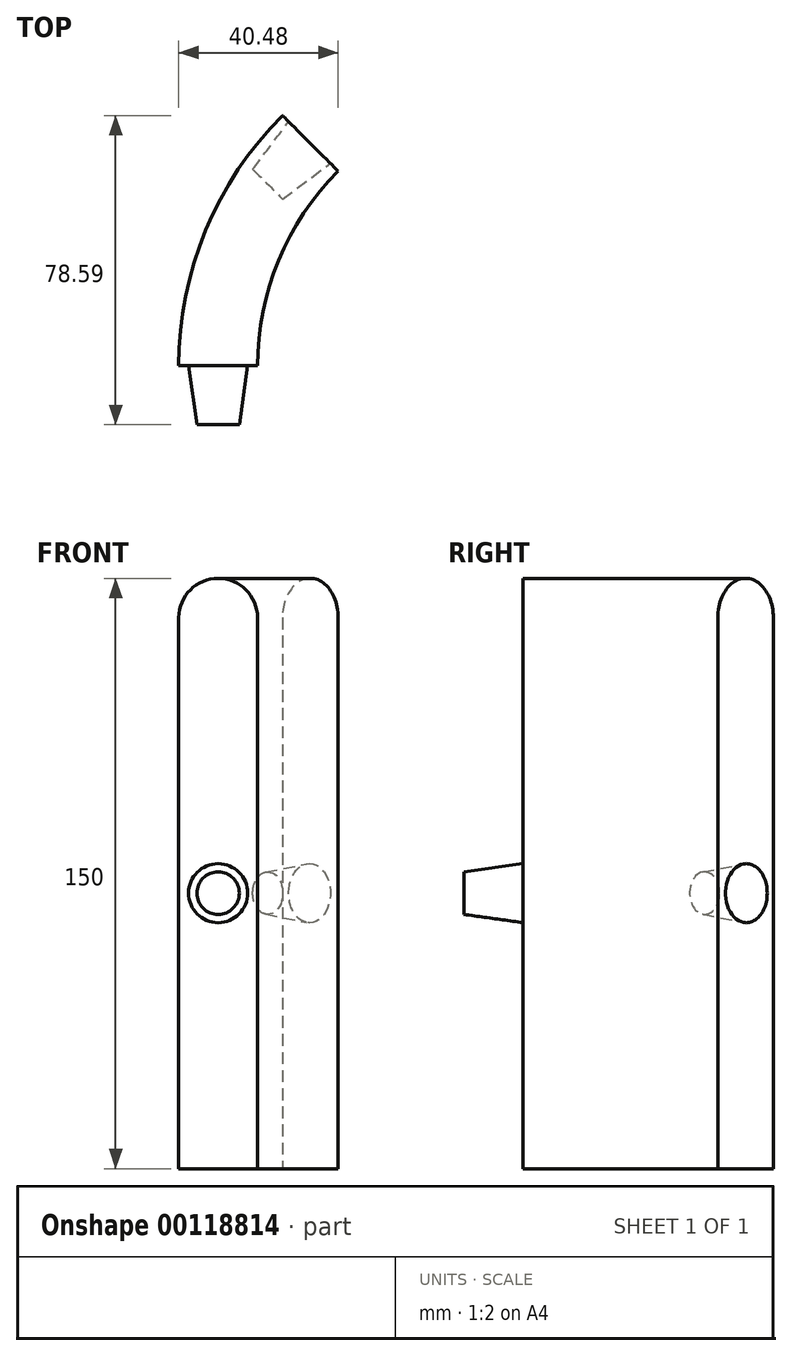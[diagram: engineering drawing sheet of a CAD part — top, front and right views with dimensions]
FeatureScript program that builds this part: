
annotation { "Feature Type Name" : "Feature", "Feature Type Description" : "" }
export const myFeature = defineFeature(function(context is Context, id is Id, definition is map)
    precondition{}
    {
        {
            var Q0;
            Q0=qCreatedBy(makeId("Front.planeOp"),FACE);
            var sketch = newSketch(context, id + "F0", { "sketchPlane" : qUnion([Q0])});
            skLineSegment(sketch, "E0", {"start": v(127.32, 299.12) * mm, "end": v(127.32, 149.12) * mm});
            skLineSegment(sketch, "E1", {"start": v(127.32, 299.12) * mm, "end": v(37.4, 299.12) * mm});
            skLineSegment(sketch, "E2", {"start": v(37.4, 299.12) * mm, "end": v(37.4, 149.12) * mm});
            skLineSegment(sketch, "E3", {"start": v(37.4, 149.12) * mm, "end": v(127.32, 149.12) * mm});
            skSolve(sketch);
        }
        {
            var Q0;
            Q0=makeQuery(id+"F0.imprint","IMPRINT",FACE,{"disambiguationData":[TD([[makeQuery(id+"F0.imprint","IMPRINT",EDGE,{"derivedFrom":sQuery(id+"F0.wireOp",EDGE,"qIKZoeJY-TQep-c7Ri-jmz6-qnDqXJ4BGPkj")}),1.0]])]});
            var Q1;
            Q1=makeQuery(id+"F0.imprint","IMPRINT",FACE,{"disambiguationData":[TD([[makeQuery(id+"F0.imprint","IMPRINT",EDGE,{"derivedFrom":sQuery(id+"F0.wireOp",EDGE,"E0")}),-1.0]])]});
            var Q2;
            Q2=sQuery(id+"F0.wireOp",EDGE,"E0");
            revolve(context, id + "F1", {"entities" : qUnion([Q0, Q1]), "axis" : qUnion([Q2]), "revolveType" : RevolveType.ONE_DIRECTION, "angle" : 45 * degree});
        }
        {
            var Q0;
            Q0=makeQuery(id+"F1.opRevolve","CAP_FACE",FACE,{"disambiguationData":[OSD([sQuery(id+"F0.wireOp",EDGE,"c1a47f16-03cb-4326-a7fb-4da27e49267e"),sQuery(id+"F0.wireOp",EDGE,"0445b6aa-1599-4f51-a42e-cd0f4c540e00"),sQuery(id+"F0.wireOp",EDGE,"2b562399-184e-4d8c-bb95-a8394558efe5.trimOffspring"),sQuery(id+"F0.wireOp",EDGE,"qIKZoeJY-TQep-c7Ri-jmz6-qnDqXJ4BGPkj"),sQuery(id+"F0.wireOp",EDGE,"5GoxPhpb-W2qU-YVQz-mgj7-7G05RjJSTRpR"),sQuery(id+"F0.wireOp",EDGE,"W7TmGzvV-SRVJ-wapx-RxKG-6s7Lfqn86I50"),sQuery(id+"F0.wireOp",EDGE,"FrPlEDyA-e7Am-JMK7-J0is-8kwWFS23w3qv")])],"isStart":false});
            var Q1;
            Q1=makeQuery(id+"F1.opRevolve","CAP_FACE",FACE,{"disambiguationData":[OSD([sQuery(id+"F0.wireOp",EDGE,"c1a47f16-03cb-4326-a7fb-4da27e49267e"),sQuery(id+"F0.wireOp",EDGE,"0445b6aa-1599-4f51-a42e-cd0f4c540e00"),sQuery(id+"F0.wireOp",EDGE,"2b562399-184e-4d8c-bb95-a8394558efe5.trimOffspring"),sQuery(id+"F0.wireOp",EDGE,"qIKZoeJY-TQep-c7Ri-jmz6-qnDqXJ4BGPkj"),sQuery(id+"F0.wireOp",EDGE,"5GoxPhpb-W2qU-YVQz-mgj7-7G05RjJSTRpR"),sQuery(id+"F0.wireOp",EDGE,"W7TmGzvV-SRVJ-wapx-RxKG-6s7Lfqn86I50"),sQuery(id+"F0.wireOp",EDGE,"FrPlEDyA-e7Am-JMK7-J0is-8kwWFS23w3qv")])],"isStart":true});
            var Q2;
            Q2=makeQuery(id+"F1.opRevolve","SWEPT_FACE",FACE,{"disambiguationData":[OSD([sQuery(id+"F0.wireOp",EDGE,"qIKZoeJY-TQep-c7Ri-jmz6-qnDqXJ4BGPkj")])]});
            var Q3;
            Q3=makeQuery(id+"F1.opRevolve","SWEPT_FACE",FACE,{"disambiguationData":[OSD([sQuery(id+"F0.wireOp",EDGE,"FrPlEDyA-e7Am-JMK7-J0is-8kwWFS23w3qv")])]});
            var Q4;
            Q4=makeQuery(id+"F1.opRevolve","SWEPT_FACE",FACE,{"disambiguationData":[OSD([sQuery(id+"F0.wireOp",EDGE,"Zfw3s35M-H7I7-ctV8-WwCO-TXvZiI164tsA")])]});
            var Q5;
            Q5=makeQuery(id+"F1.opRevolve","SWEPT_FACE",FACE,{"disambiguationData":[OSD([sQuery(id+"F0.wireOp",EDGE,"DxNpelhW-NPha-Za65-5rby-Dc9gSIxmAqf3")])]});
            var Q6;
            Q6=makeQuery(id+"F1.opRevolve","CAP_FACE",FACE,{"disambiguationData":[OSD([sQuery(id+"F0.wireOp",EDGE,"E0"),sQuery(id+"F0.wireOp",EDGE,"h8w9ds9V-v6di-2uzp-dC4j-q0jaSeQ5vev1"),sQuery(id+"F0.wireOp",EDGE,"rqYKbdp3-fYyZ-YRGA-wxHp-ysZJsVzrtoBV"),sQuery(id+"F0.wireOp",EDGE,"CGmn5kAD-aOFs-twpu-ufA2-BfELl45xMEkJ")])],"isStart":true});
            var Q7;
            Q7=makeQuery(id+"F1.opRevolve","CAP_FACE",FACE,{"disambiguationData":[OSD([sQuery(id+"F0.wireOp",EDGE,"E0"),sQuery(id+"F0.wireOp",EDGE,"h8w9ds9V-v6di-2uzp-dC4j-q0jaSeQ5vev1"),sQuery(id+"F0.wireOp",EDGE,"rqYKbdp3-fYyZ-YRGA-wxHp-ysZJsVzrtoBV"),sQuery(id+"F0.wireOp",EDGE,"CGmn5kAD-aOFs-twpu-ufA2-BfELl45xMEkJ")])],"isStart":false});
            var Q8;
            Q8=makeQuery(id+"F1.opRevolve","SWEPT_FACE",FACE,{"disambiguationData":[OSD([sQuery(id+"F0.wireOp",EDGE,"CGmn5kAD-aOFs-twpu-ufA2-BfELl45xMEkJ")])]});
            var Q9;
            Q9=makeQuery(id+"F1.opRevolve","SWEPT_FACE",FACE,{"disambiguationData":[OSD([sQuery(id+"F0.wireOp",EDGE,"rqYKbdp3-fYyZ-YRGA-wxHp-ysZJsVzrtoBV")])]});
            var Q10;
            Q10=makeQuery(id+"F1.opRevolve","SWEPT_FACE",FACE,{"disambiguationData":[OSD([sQuery(id+"F0.wireOp",EDGE,"E3")])]});
            var Q11;
            Q11=makeQuery(id+"F1.opRevolve","SWEPT_FACE",FACE,{"disambiguationData":[OSD([sQuery(id+"F0.wireOp",EDGE,"E1")])]});
            shell(context, id + "F2", {"entities" : qUnion([Q0, Q1, Q2, Q3, Q4, Q5, Q6, Q7, Q8, Q9, Q10, Q11]), "thickness" : 20 * mm});
        }
        {
            var Q0;
            Q0=makeQuery(id+"F1.opRevolve","CAP_FACE",FACE,{"disambiguationData":[OSD([sQuery(id+"F0.wireOp",EDGE,"E0"),sQuery(id+"F0.wireOp",EDGE,"h8w9ds9V-v6di-2uzp-dC4j-q0jaSeQ5vev1"),sQuery(id+"F0.wireOp",EDGE,"rqYKbdp3-fYyZ-YRGA-wxHp-ysZJsVzrtoBV"),sQuery(id+"F0.wireOp",EDGE,"CGmn5kAD-aOFs-twpu-ufA2-BfELl45xMEkJ")])],"isStart":true});
            var sketch = newSketch(context, id + "F3", { "sketchPlane" : qUnion([Q0])});
            skCircle(sketch, "E4", {"center": v(47.4, 219.12) * mm, "radius": 7.5 * mm});
            skSolve(sketch);
        }
        {
            var Q0;
            Q0 = qSketchRegion(id + "F3", true);
            extrude(context, id + "F4", {"entities" : qUnion([Q0]), "operationType" : NewBodyOperationType.ADD, "depth" : 15 * mm, "hasDraft" : true, "draftAngle" : 8 * degree, "draftPullDirection" : true});
        }
        {
            var Q0;
            Q0=makeQuery(id+"F1.opRevolve","CAP_FACE",FACE,{"disambiguationData":[OSD([sQuery(id+"F0.wireOp",EDGE,"E0"),sQuery(id+"F0.wireOp",EDGE,"h8w9ds9V-v6di-2uzp-dC4j-q0jaSeQ5vev1"),sQuery(id+"F0.wireOp",EDGE,"rqYKbdp3-fYyZ-YRGA-wxHp-ysZJsVzrtoBV"),sQuery(id+"F0.wireOp",EDGE,"CGmn5kAD-aOFs-twpu-ufA2-BfELl45xMEkJ")])],"isStart":false});
            var sketch = newSketch(context, id + "F5", { "sketchPlane" : qUnion([Q0])});
            skCircle(sketch, "E5", {"center": v(-9.82, 219.12) * mm, "radius": 7.5 * mm});
            skSolve(sketch);
        }
        {
            var Q0;
            Q0 = qSketchRegion(id + "F5", true);
            extrude(context, id + "F6", {"entities" : qUnion([Q0]), "operationType" : NewBodyOperationType.REMOVE, "oppositeDirection" : true, "depth" : 15 * mm, "hasDraft" : true, "draftAngle" : 8 * degree, "draftPullDirection" : true});
        }
        {
            var Q0;
            Q0=makeQuery(id+"F1.opRevolve","SWEPT_EDGE",EDGE,{"disambiguationData":[OSD([sQuery(id+"F0.wireOp",EDGE,"E1"),sQuery(id+"F0.wireOp",EDGE,"E2")])]});
            var Q1;
            Q1=makeQuery(id+"F2.opShell","OFFSET_EDGE",EDGE,{"disambiguationData":[OSD([sQuery(id+"F0.wireOp",EDGE,"E1"),sQuery(id+"F0.wireOp",EDGE,"E2")])]});
            fillet(context, id + "F7", {"entities" : qUnion([Q0, Q1]), "radius" : 10 * mm, "tangentPropagation" : true, "allowEdgeOverflow" : false});
        }
    });
